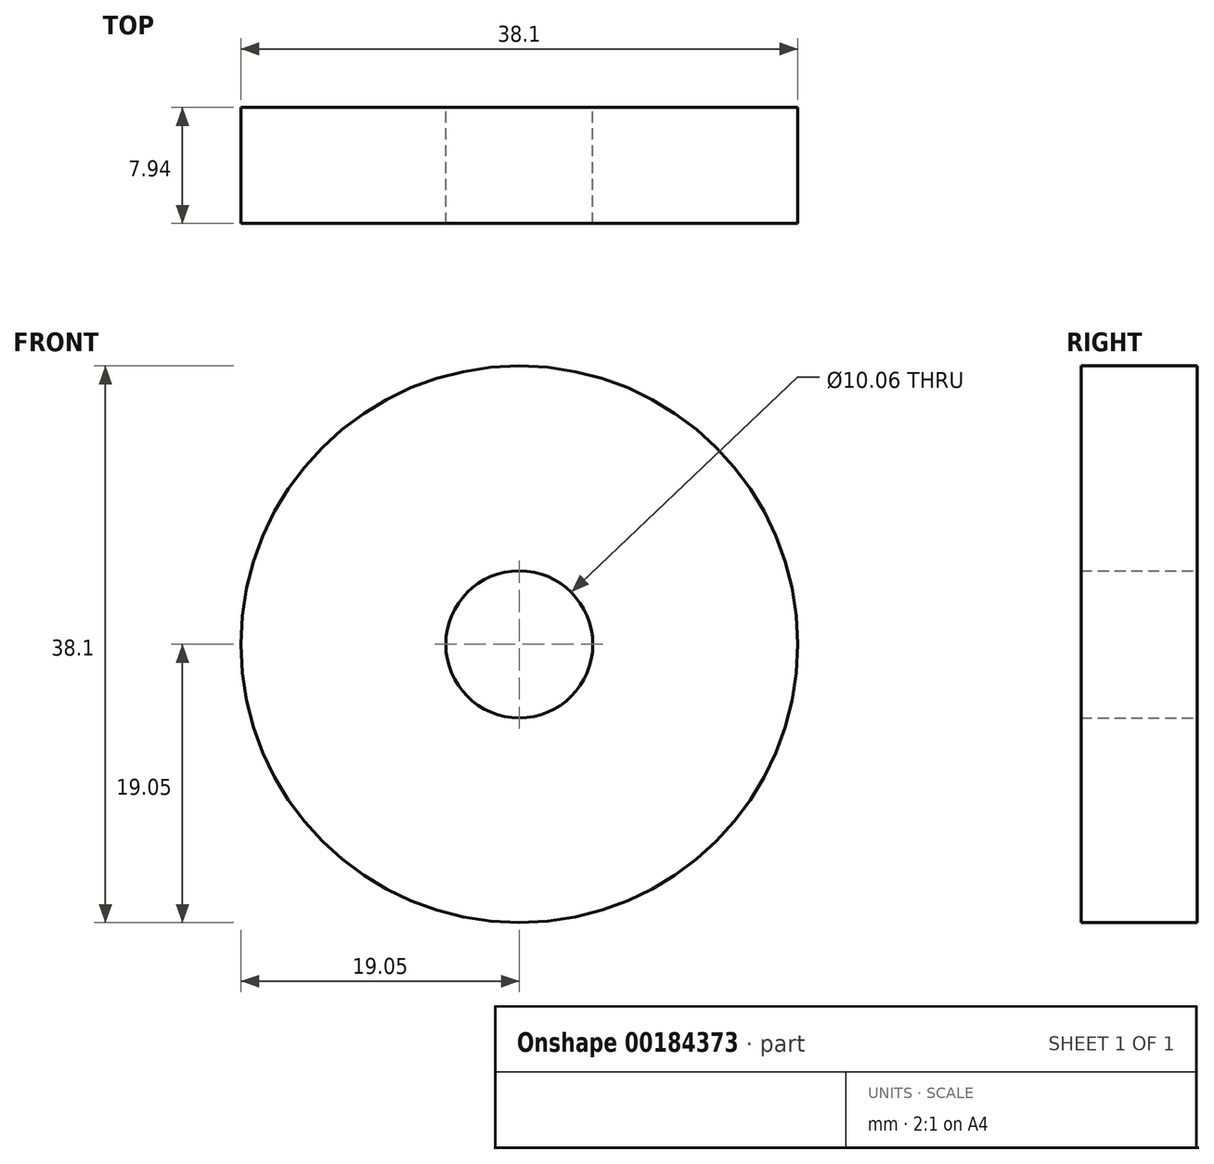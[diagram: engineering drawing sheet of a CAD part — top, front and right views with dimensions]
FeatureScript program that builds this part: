
annotation { "Feature Type Name" : "Feature", "Feature Type Description" : "" }
export const myFeature = defineFeature(function(context is Context, id is Id, definition is map)
    precondition{}
    {
        {
            var Q0;
            Q0=qCreatedBy(makeId("Front.planeOp"),FACE);
            var sketch = newSketch(context, id + "F0", { "sketchPlane" : qUnion([Q0])});
            skCircle(sketch, "E0", {"center": v(0, 0) * mm, "radius": 19.05 * mm});
            skCircle(sketch, "E1", {"center": v(0, 0) * mm, "radius": 5.03 * mm});
            skSolve(sketch);
        }
        {
            var Q0;
            Q0 = qSketchRegion(id + "F0", true);
            extrude(context, id + "F1", {"entities" : qUnion([Q0]), "depth" : 7.94 * mm});
        }
    });
